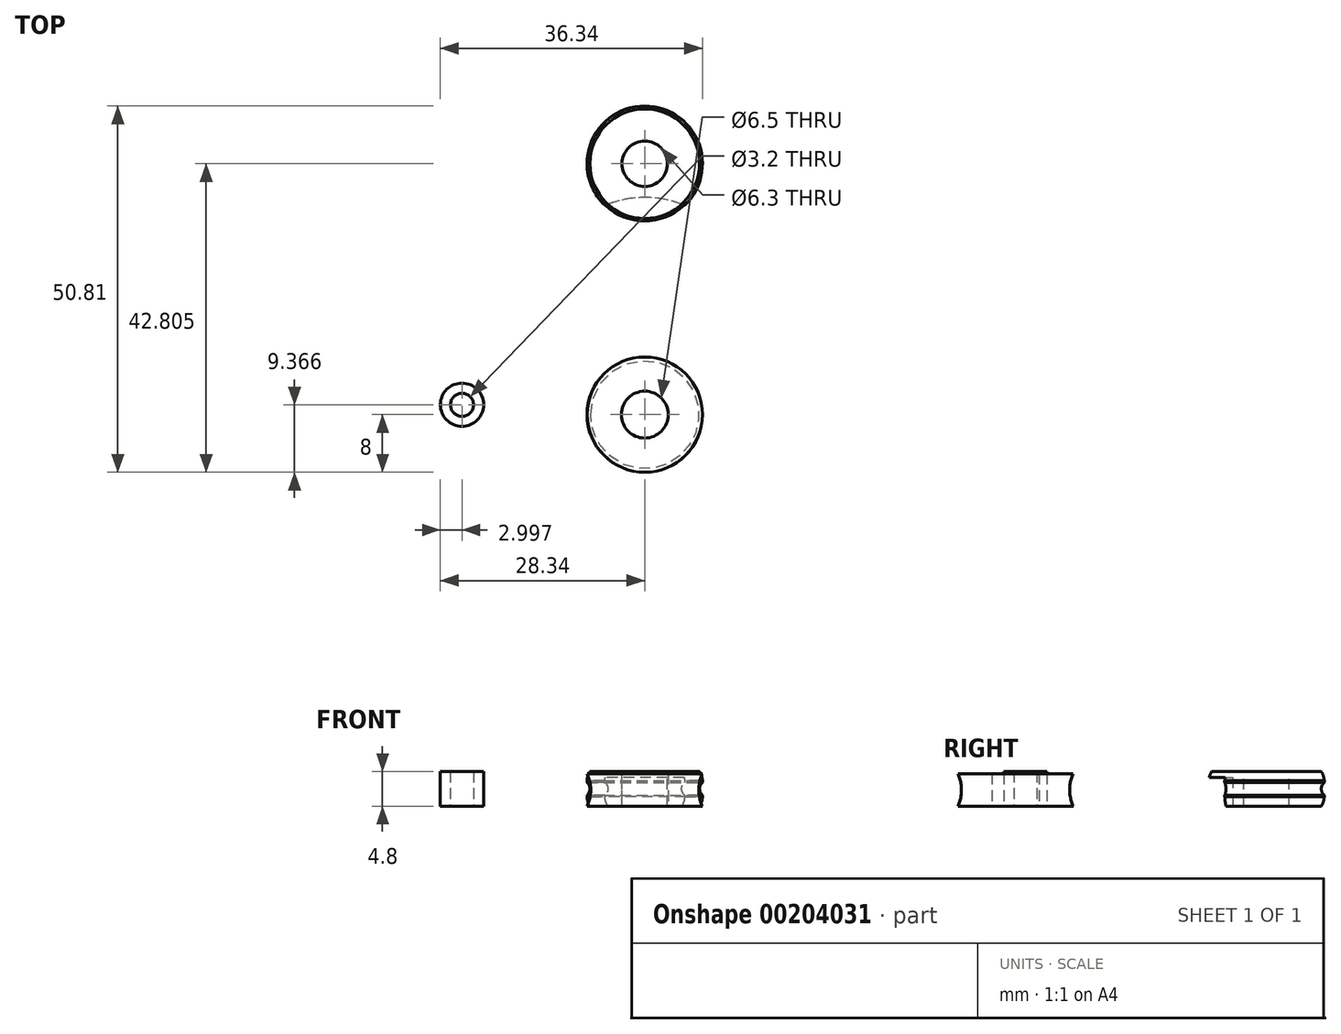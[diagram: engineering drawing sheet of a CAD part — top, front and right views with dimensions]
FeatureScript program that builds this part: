
annotation { "Feature Type Name" : "Feature", "Feature Type Description" : "" }
export const myFeature = defineFeature(function(context is Context, id is Id, definition is map)
    precondition{}
    {
        {
            var Q0;
            Q0=qCreatedBy(makeId("Top.planeOp"),FACE);
            var sketch = newSketch(context, id + "F0", { "sketchPlane" : qUnion([Q0])});
            skCircle(sketch, "E0", {"center": v(-25.34, 1.37) * mm, "radius": 3 * mm});
            skCircle(sketch, "E1", {"center": v(-25.34, 1.37) * mm, "radius": 1.6 * mm});
            skCircle(sketch, "E2", {"center": v(0, 15.76) * mm, "radius": 8 * mm});
            skCircle(sketch, "E3", {"center": v(0, 34.8) * mm, "radius": 8 * mm});
            skSolve(sketch);
        }
        {
            var Q0;
            Q0 = qSketchRegion(id + "F0", true);
            extrude(context, id + "F1", {"entities" : qUnion([Q0]), "depth" : 4 * mm});
        }
        {
            var Q0;
            Q0=makeQuery(id+"F1.opExtrude","CAP_FACE",FACE,{"disambiguationData":[OSD([sQuery(id+"F0.wireOp",EDGE,"E3")])],"isStart":false});
            extrude(context, id + "F2", {"entities" : qUnion([Q0]), "operationType" : NewBodyOperationType.ADD, "depth" : .8 * mm});
        }
        {
            var Q0;
            Q0=makeQuery(id+"F1.opExtrude","CAP_FACE",FACE,{"disambiguationData":[OSD([sQuery(id+"F0.wireOp",EDGE,"E2")])],"isStart":false});
            var sketch = newSketch(context, id + "F3", { "sketchPlane" : qUnion([Q0])});
            skCircle(sketch, "E4", {"center": v(0, 15.76) * mm, "radius": 3 * mm});
            skCircle(sketch, "E5", {"center": v(0, 34.8) * mm, "radius": 3 * mm});
            skSolve(sketch);
        }
        {
            var Q0;
            Q0 = qSketchRegion(id + "F3", true);
            extrude(context, id + "F4", {"entities" : qUnion([Q0]), "operationType" : NewBodyOperationType.REMOVE, "oppositeDirection" : true, "depth" : 25 * mm, "hasSecondDirection" : true, "secondDirectionOppositeDirection" : false, "secondDirectionDepth" : 25 * mm});
        }
        {
            var Q0;
            Q0=qCreatedBy(makeId("Top.planeOp"),FACE);
            cPlane(context, id + "F5", {"entities" : qUnion([Q0]), "cplaneType" : CPlaneType.OFFSET, "offset" : 2 * mm, "width" : 150 * mm, "height" : 150 * mm});
        }
        {
            var Q0;
            Q0=qCreatedBy(makeId("Right.planeOp"),FACE);
            var sketch = newSketch(context, id + "F6", { "sketchPlane" : qUnion([Q0])});
            skLineSegment(sketch, "E6", {"start": v(7.76, 0) * mm, "end": v(7.76, 4) * mm, "construction": true});
            skLineSegment(sketch, "E7.0", {"start": v(7.76, 4) * mm, "end": v(23.76, 4) * mm, "construction": true});
            skPoint(sketch, "E8", {"position": v(15.76, 4) * mm});
            skLineSegment(sketch, "E9", {"start": v(15.76, 4) * mm, "end": v(15.76, 2) * mm, "construction": true});
            skPoint(sketch, "E9.endSnap0", {"position": v(7.76, 2) * mm});
            skLineSegment(sketch, "E10", {"start": v(15.76, 2) * mm, "end": v(8.16, 2) * mm, "construction": true});
            skArc(sketch, "E11", {"start": v(7.76, 1.1) * mm, "mid": v(8.16, 2) * mm, "end": v(7.76, 2.9) * mm});
            skLineSegment(sketch, "E12", {"start": v(8.16, 2) * mm, "end": v(8.16, 4) * mm, "construction": true});
            skArc(sketch, "E13", {"start": v(8.16, 4) * mm, "mid": v(7.9, 3.47) * mm, "end": v(7.76, 2.9) * mm});
            skArc(sketch, "E14", {"start": v(7.76, 1.1) * mm, "mid": v(7.9, 0.53) * mm, "end": v(8.16, 0) * mm});
            skLineSegment(sketch, "E15", {"start": v(8.16, 4) * mm, "end": v(7.76, 4) * mm});
            skLineSegment(sketch, "E16", {"start": v(7.76, 4) * mm, "end": v(1.39, 4) * mm});
            skLineSegment(sketch, "E17", {"start": v(1.39, 4) * mm, "end": v(1.39, 0) * mm});
            skLineSegment(sketch, "E18", {"start": v(1.39, 0) * mm, "end": v(8.16, 0) * mm});
            skSolve(sketch);
        }
        {
            var Q0;
            Q0 = qSketchRegion(id + "F6", true);
            var Q1;
            Q1=sQuery(id+"F6.wireOp",EDGE,"E9");
            revolve(context, id + "F7", {"operationType" : NewBodyOperationType.REMOVE, "entities" : qUnion([Q0]), "axis" : qUnion([Q1]), "revolveType" : RevolveType.FULL, "oppositeDirection" : true});
        }
        {
            var Q0;
            Q0=qCreatedBy(makeId("Top.planeOp"),FACE);
            cPlane(context, id + "F8", {"entities" : qUnion([Q0]), "cplaneType" : CPlaneType.OFFSET, "offset" : (4.8 / 2) * mm, "width" : 150 * mm, "height" : 150 * mm});
        }
        {
            var Q0;
            Q0=qCreatedBy(makeId("Right.planeOp"),FACE);
            var sketch = newSketch(context, id + "F9", { "sketchPlane" : qUnion([Q0])});
            skLineSegment(sketch, "E19", {"start": v(26.8, 0) * mm, "end": v(26.8, 4.8) * mm, "construction": true});
            skLineSegment(sketch, "E20.0", {"start": v(26.8, 4.8) * mm, "end": v(42.8, 4.8) * mm, "construction": true});
            skLineSegment(sketch, "E21", {"start": v(34.8, 4.8) * mm, "end": v(34.8, 2.4) * mm, "construction": true});
            skPoint(sketch, "E21.endSnap0", {"position": v(26.8, 2.4) * mm});
            skLineSegment(sketch, "E22", {"start": v(34.8, 2.4) * mm, "end": v(27.2, 2.4) * mm, "construction": true});
            skArc(sketch, "E23", {"start": v(26.8, 1.5) * mm, "mid": v(27.2, 2.4) * mm, "end": v(26.8, 3.3) * mm});
            skLineSegment(sketch, "E24", {"start": v(27.2, 2.4) * mm, "end": v(27.2, 4.8) * mm, "construction": true});
            skLineSegment(sketch, "E25", {"start": v(27.2, 2.4) * mm, "end": v(27.2, 0) * mm, "construction": true});
            skArc(sketch, "E26", {"start": v(27.2, 4.8) * mm, "mid": v(26.9, 4.08) * mm, "end": v(26.8, 3.3) * mm});
            skArc(sketch, "E27", {"start": v(26.8, 1.5) * mm, "mid": v(26.9, 0.72) * mm, "end": v(27.2, 0) * mm});
            skArc(sketch, "E28", {"start": v(27.2, 4.8) * mm, "mid": v(9.2, 2.4) * mm, "end": v(27.2, 0) * mm});
            skSolve(sketch);
        }
        {
            var Q0;
            Q0 = qSketchRegion(id + "F9", true);
            var Q1;
            Q1=sQuery(id+"F9.wireOp",EDGE,"E21");
            revolve(context, id + "F10", {"operationType" : NewBodyOperationType.REMOVE, "entities" : qUnion([Q0]), "axis" : qUnion([Q1]), "revolveType" : RevolveType.FULL, "oppositeDirection" : true});
        }
        {
            var Q0;
            Q0=makeQuery(id+"F1.opExtrude","CAP_FACE",FACE,{"disambiguationData":[OSD([sQuery(id+"F0.wireOp",EDGE,"E0"),sQuery(id+"F0.wireOp",EDGE,"E1")])],"isStart":false});
            extrude(context, id + "F11", {"entities" : qUnion([Q0]), "operationType" : NewBodyOperationType.ADD, "depth" : .8 * mm});
        }
        {
            var Q0;
            Q0=makeQuery(id+"F2.opExtrude","CAP_FACE",FACE,{"disambiguationData":[OSD([sQuery(id+"F0.wireOp",EDGE,"E3")])],"isStart":false});
            var sketch = newSketch(context, id + "F12", { "sketchPlane" : qUnion([Q0])});
            skCircle(sketch, "E29", {"center": v(0, 34.8) * mm, "radius": 3.15 * mm});
            skCircle(sketch, "E30.0", {"center": v(0, 15.76) * mm, "radius": 3 * mm, "construction": true});
            skCircle(sketch, "E31", {"center": v(0, 15.76) * mm, "radius": 3.15 * mm});
            skSolve(sketch);
        }
        {
            var Q0;
            Q0 = qSketchRegion(id + "F12", true);
            extrude(context, id + "F13", {"entities" : qUnion([Q0]), "operationType" : NewBodyOperationType.REMOVE, "oppositeDirection" : true, "depth" : 25 * mm, "hasSecondDirection" : true, "secondDirectionOppositeDirection" : false, "secondDirectionDepth" : 25 * mm});
        }
        {
            var Q0;
            Q0=qCreatedBy(makeId("Top.planeOp"),FACE);
            var sketch = newSketch(context, id + "F14", { "sketchPlane" : qUnion([Q0])});
            skCircle(sketch, "E32", {"center": v(0, 0) * mm, "radius": 8 * mm});
            skCircle(sketch, "E33", {"center": v(0, 0) * mm, "radius": 3.25 * mm});
            skSolve(sketch);
        }
        {
            var Q0;
            Q0 = qSketchRegion(id + "F14", true);
            extrude(context, id + "F15", {"entities" : qUnion([Q0]), "depth" : 4.5 * mm});
        }
        {
            var Q0;
            Q0=qCreatedBy(makeId("Right.planeOp"),FACE);
            var sketch = newSketch(context, id + "F16", { "sketchPlane" : qUnion([Q0])});
            skLineSegment(sketch, "E34", {"start": v(-8, 0) * mm, "end": v(-8, 4.52) * mm, "construction": true});
            skLineSegment(sketch, "E35.0", {"start": v(-8, 4.5) * mm, "end": v(8, 4.5) * mm, "construction": true});
            skLineSegment(sketch, "E36", {"start": v(-7.5, 2.26) * mm, "end": v(7.5, 2.26) * mm, "construction": true});
            skPoint(sketch, "E36.startSnap0", {"position": v(-8, 2.26) * mm});
            skPoint(sketch, "E37", {"position": v(0, 2.26) * mm});
            skArc(sketch, "E38", {"start": v(-8, 0) * mm, "mid": v(-7.5, 2.26) * mm, "end": v(-8, 4.52) * mm});
            skArc(sketch, "E39", {"start": v(-8, 4.52) * mm, "mid": v(-17.87, 2.26) * mm, "end": v(-8, 0) * mm});
            skLineSegment(sketch, "E40", {"start": v(0, 4.5) * mm, "end": v(0, 0) * mm, "construction": true});
            skSolve(sketch);
        }
        {
            var Q0;
            Q0 = qSketchRegion(id + "F16", true);
            var Q1;
            Q1=sQuery(id+"F16.wireOp",EDGE,"E40");
            revolve(context, id + "F17", {"operationType" : NewBodyOperationType.REMOVE, "entities" : qUnion([Q0]), "axis" : qUnion([Q1]), "revolveType" : RevolveType.FULL, "oppositeDirection" : true});
        }
    });
